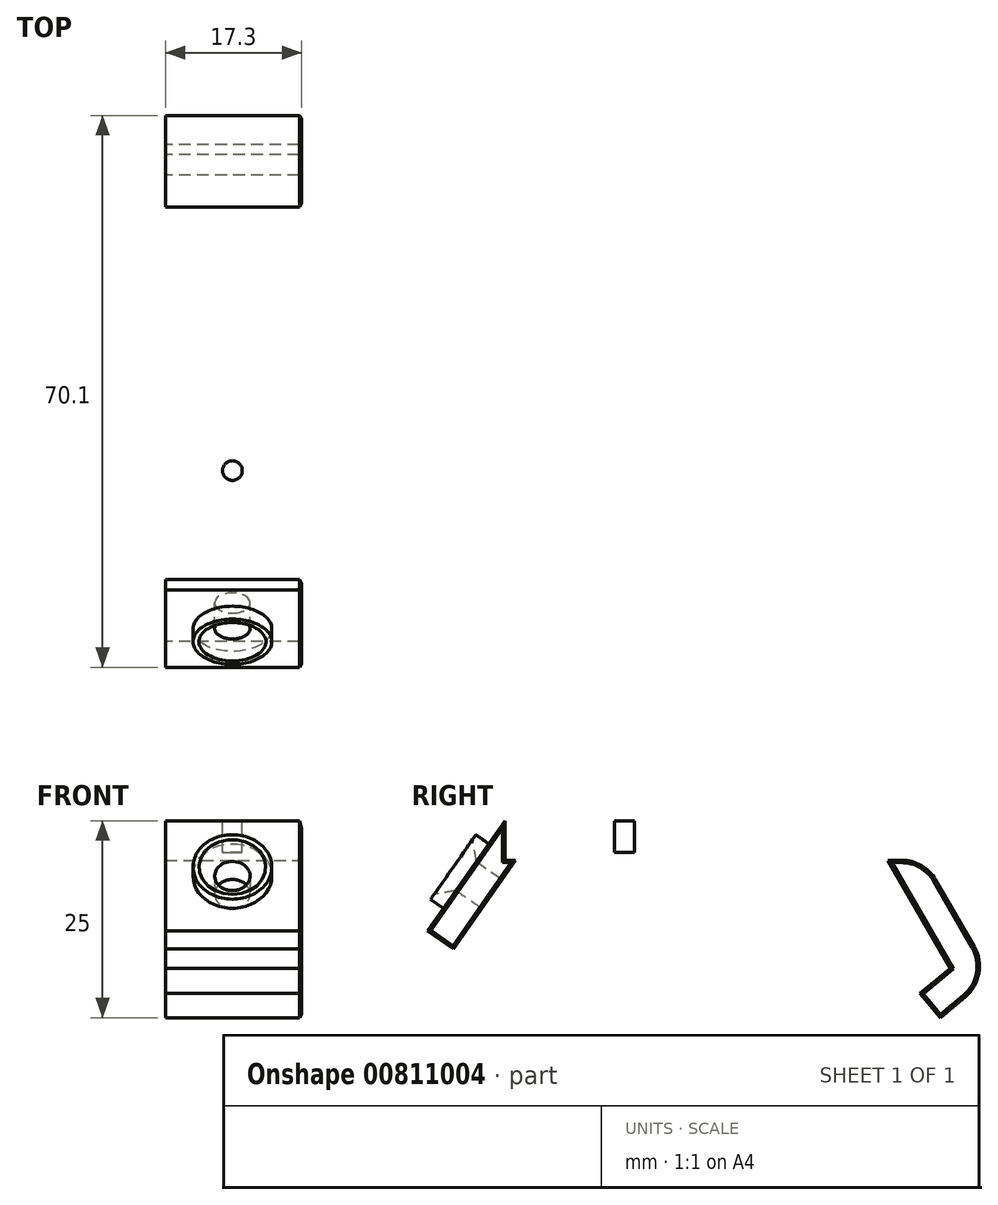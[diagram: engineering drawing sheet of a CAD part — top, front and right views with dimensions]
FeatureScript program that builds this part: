
annotation { "Feature Type Name" : "Feature", "Feature Type Description" : "" }
export const myFeature = defineFeature(function(context is Context, id is Id, definition is map)
    precondition{}
    {
        {
            var Q0;
            Q0=qCreatedBy(makeId("Right.planeOp"),FACE);
            var sketch = newSketch(context, id + "F0", { "sketchPlane" : qUnion([Q0])});
            skLineSegment(sketch, "E0", {"start": v(-23.86, -20.05) * mm, "end": v(-15.26, -7.76) * mm});
            skLineSegment(sketch, "E1", {"start": v(-15.26, -7.76) * mm, "end": v(30.74, -7.76) * mm});
            skLineSegment(sketch, "E2", {"start": v(30.74, -7.76) * mm, "end": v(39.24, -22.49) * mm});
            skLineSegment(sketch, "E3", {"start": v(39.24, -22.49) * mm, "end": v(35.41, -25.7) * mm});
            skLineSegment(sketch, "E4", {"start": v(35.41, -25.7) * mm, "end": v(37.98, -28.76) * mm});
            skLineSegment(sketch, "E5", {"start": v(37.98, -28.76) * mm, "end": v(44.39, -23.4) * mm});
            skLineSegment(sketch, "E6", {"start": v(44.39, -23.4) * mm, "end": v(33.05, -3.76) * mm});
            skLineSegment(sketch, "E7", {"start": v(33.05, -3.76) * mm, "end": v(-17.34, -3.76) * mm});
            skLineSegment(sketch, "E8", {"start": v(-17.34, -3.76) * mm, "end": v(-27.14, -17.76) * mm});
            skLineSegment(sketch, "E9", {"start": v(-27.14, -17.76) * mm, "end": v(-23.86, -20.05) * mm});
            skSolve(sketch);
        }
        {
            var Q0;
            Q0=makeQuery(id+"F0.imprint","IMPRINT",FACE,{"disambiguationData":[TD([[makeQuery(id+"F0.imprint","IMPRINT",EDGE,{"derivedFrom":sQuery(id+"F0.wireOp",EDGE,"E0")}),1.0]])]});
            extrude(context, id + "F1", {"entities" : qUnion([Q0]), "depth" : 17 * mm, "offsetDistance" : 25 * mm});
        }
        {
            var Q0;
            Q0=makeQuery(id+"F1.opExtrude","SWEPT_FACE",FACE,{"disambiguationData":[OSD([sQuery(id+"F0.wireOp",EDGE,"E8")])]});
            var sketch = newSketch(context, id + "F2", { "sketchPlane" : qUnion([Q0])});
            skLineSegment(sketch, "E10", {"start": v(0, -13.03) * mm, "end": v(17, -30.11) * mm, "construction": true});
            skLineSegment(sketch, "E11", {"start": v(17, -13.03) * mm, "end": v(0, -30.11) * mm, "construction": true});
            skCircle(sketch, "E12", {"center": v(8.5, -21.57) * mm, "radius": 2.25 * mm});
            skCircle(sketch, "E13", {"center": v(8.5, -21.57) * mm, "radius": 5 * mm});
            skSolve(sketch);
        }
        {
            var Q0;
            Q0=makeQuery(id+"F2.imprint","IMPRINT",FACE,{"disambiguationData":[TD([[makeQuery(id+"F2.imprint","IMPRINT",EDGE,{"derivedFrom":sQuery(id+"F2.wireOp",EDGE,"E12")}),-1.0]])]});
            extrude(context, id + "F3", {"entities" : qUnion([Q0]), "operationType" : NewBodyOperationType.ADD, "depth" : 2 * mm, "offsetDistance" : 25 * mm});
        }
        {
            var Q0;
            Q0=makeQuery(id+"F3.boolean.opBoolean","SPLIT",FACE,{"disambiguationData":[TD([makeQuery(id+"F3.opExtrude","SWEPT_FACE",FACE,{"disambiguationData":[OSD([sQuery(id+"F2.wireOp",EDGE,"E12")])]})])],"derivedFrom":makeQuery(id+"F1.opExtrude","SWEPT_FACE",FACE,{"disambiguationData":[OSD([sQuery(id+"F0.wireOp",EDGE,"E8")])]})});
            extrude(context, id + "F4", {"entities" : qUnion([Q0]), "operationType" : NewBodyOperationType.REMOVE, "oppositeDirection" : true, "depth" : 10 * mm, "offsetDistance" : 25 * mm});
        }
        {
            var Q0;
            Q0=makeQuery(id+"F1.opExtrude","SWEPT_FACE",FACE,{"disambiguationData":[OSD([sQuery(id+"F0.wireOp",EDGE,"E7")])]});
            var sketch = newSketch(context, id + "F5", { "sketchPlane" : qUnion([Q0])});
            skLineSegment(sketch, "E14", {"start": v(0, 33.05) * mm, "end": v(17, -17.34) * mm, "construction": true});
            skLineSegment(sketch, "E15", {"start": v(17, 33.05) * mm, "end": v(0, -17.34) * mm, "construction": true});
            skCircle(sketch, "E16", {"center": v(8.5, 7.86) * mm, "radius": 1.25 * mm});
            skLineSegment(sketch, "E17", {"start": v(8.5, 33.05) * mm, "end": v(8.5, 7.86) * mm, "construction": true});
            skLineSegment(sketch, "E18", {"start": v(0, 7.86) * mm, "end": v(17, 7.86) * mm, "construction": true});
            skLineSegment(sketch, "E19", {"start": v(0, 17.86) * mm, "end": v(17, 17.86) * mm, "construction": true});
            skCircle(sketch, "E20", {"center": v(8.5, 17.86) * mm, "radius": 1.25 * mm});
            skCircle(sketch, "E21.MirrorC", {"center": v(8.5, -2.14) * mm, "radius": 1.25 * mm});
            skSolve(sketch);
        }
        {
            var Q0;
            Q0=makeQuery(id+"F5.imprint","IMPRINT",FACE,{"disambiguationData":[TD([[makeQuery(id+"F5.imprint","IMPRINT",EDGE,{"derivedFrom":sQuery(id+"F5.wireOp",EDGE,"E16")}),1.0]])]});
            var Q1;
            Q1=makeQuery(id+"F5.imprint","IMPRINT",FACE,{"disambiguationData":[TD([[makeQuery(id+"F5.imprint","IMPRINT",EDGE,{"derivedFrom":sQuery(id+"F5.wireOp",EDGE,"E20")}),1.0]])]});
            var Q2;
            Q2=makeQuery(id+"F5.imprint","IMPRINT",FACE,{"disambiguationData":[TD([[makeQuery(id+"F5.imprint","IMPRINT",EDGE,{"derivedFrom":sQuery(id+"F5.wireOp",EDGE,"E21.MirrorC")}),-1.0]])]});
            extrude(context, id + "F6", {"entities" : qUnion([Q0, Q1, Q2]), "operationType" : NewBodyOperationType.REMOVE, "oppositeDirection" : true, "depth" : 5 * mm, "offsetDistance" : 25 * mm});
        }
        {
            var Q0;
            Q0=makeQuery(id+"F3.opExtrude","CAP_EDGE",EDGE,{"disambiguationData":[OSD([sQuery(id+"F2.wireOp",EDGE,"E13")])],"isStart":true});
            var Q1;
            Q1=makeQuery(id+"F3.opExtrude","CAP_EDGE",EDGE,{"disambiguationData":[OSD([sQuery(id+"F2.wireOp",EDGE,"E12")])],"isStart":false});
            chamfer(context, id + "F7", {"entities" : qUnion([Q0, Q1]), "width" : 2 * mm, "tangentPropagation" : true});
        }
        {
            var Q0;
            Q0=makeQuery(id+"F1.opExtrude","SWEPT_EDGE",EDGE,{"disambiguationData":[OSD([sQuery(id+"F0.wireOp",EDGE,"E7"),sQuery(id+"F0.wireOp",EDGE,"E8")])]});
            var Q1;
            Q1=makeQuery(id+"F1.opExtrude","SWEPT_EDGE",EDGE,{"disambiguationData":[OSD([sQuery(id+"F0.wireOp",EDGE,"E0"),sQuery(id+"F0.wireOp",EDGE,"E1")])]});
            var Q2;
            Q2=makeQuery(id+"F1.opExtrude","SWEPT_EDGE",EDGE,{"disambiguationData":[OSD([sQuery(id+"F0.wireOp",EDGE,"E5"),sQuery(id+"F0.wireOp",EDGE,"E6")])]});
            var Q3;
            Q3=makeQuery(id+"F1.opExtrude","SWEPT_EDGE",EDGE,{"disambiguationData":[OSD([sQuery(id+"F0.wireOp",EDGE,"E6"),sQuery(id+"F0.wireOp",EDGE,"E7")])]});
            var Q4;
            Q4=makeQuery(id+"F1.opExtrude","SWEPT_EDGE",EDGE,{"disambiguationData":[OSD([sQuery(id+"F0.wireOp",EDGE,"E1"),sQuery(id+"F0.wireOp",EDGE,"E2")])]});
            fillet(context, id + "F8", {"entities" : qUnion([Q0, Q1, Q2, Q3, Q4]), "radius" : 5 * mm, "tangentPropagation" : true, "allowEdgeOverflow" : false});
        }
        {
            var Q0;
            Q0=makeQuery(id+"F1.opExtrude","CAP_FACE",FACE,{"disambiguationData":[OSD([sQuery(id+"F0.wireOp",EDGE,"E0"),sQuery(id+"F0.wireOp",EDGE,"E1"),sQuery(id+"F0.wireOp",EDGE,"E2"),sQuery(id+"F0.wireOp",EDGE,"E3"),sQuery(id+"F0.wireOp",EDGE,"E4"),sQuery(id+"F0.wireOp",EDGE,"E5"),sQuery(id+"F0.wireOp",EDGE,"E6"),sQuery(id+"F0.wireOp",EDGE,"E7"),sQuery(id+"F0.wireOp",EDGE,"E8"),sQuery(id+"F0.wireOp",EDGE,"E9")])],"isStart":false});
            extrude(context, id + "F9", {"entities" : qUnion([Q0]), "operationType" : NewBodyOperationType.ADD, "depth" : 0.3 * mm, "offsetDistance" : 25 * mm});
        }
        {
            var Q0;
            Q0=makeQuery(id+"F9.opExtrude","CAP_FACE",FACE,{"disambiguationData":[OSD([sQuery(id+"F0.wireOp",EDGE,"E0"),sQuery(id+"F0.wireOp",EDGE,"E1"),sQuery(id+"F0.wireOp",EDGE,"E2"),sQuery(id+"F0.wireOp",EDGE,"E3"),sQuery(id+"F0.wireOp",EDGE,"E4"),sQuery(id+"F0.wireOp",EDGE,"E5"),sQuery(id+"F0.wireOp",EDGE,"E6"),sQuery(id+"F0.wireOp",EDGE,"E7"),sQuery(id+"F0.wireOp",EDGE,"E8"),sQuery(id+"F0.wireOp",EDGE,"E9")])],"isStart":false});
            chamfer(context, id + "F10", {"entities" : qUnion([Q0]), "width" : 0.3 * mm, "tangentPropagation" : true});
        }
    });
